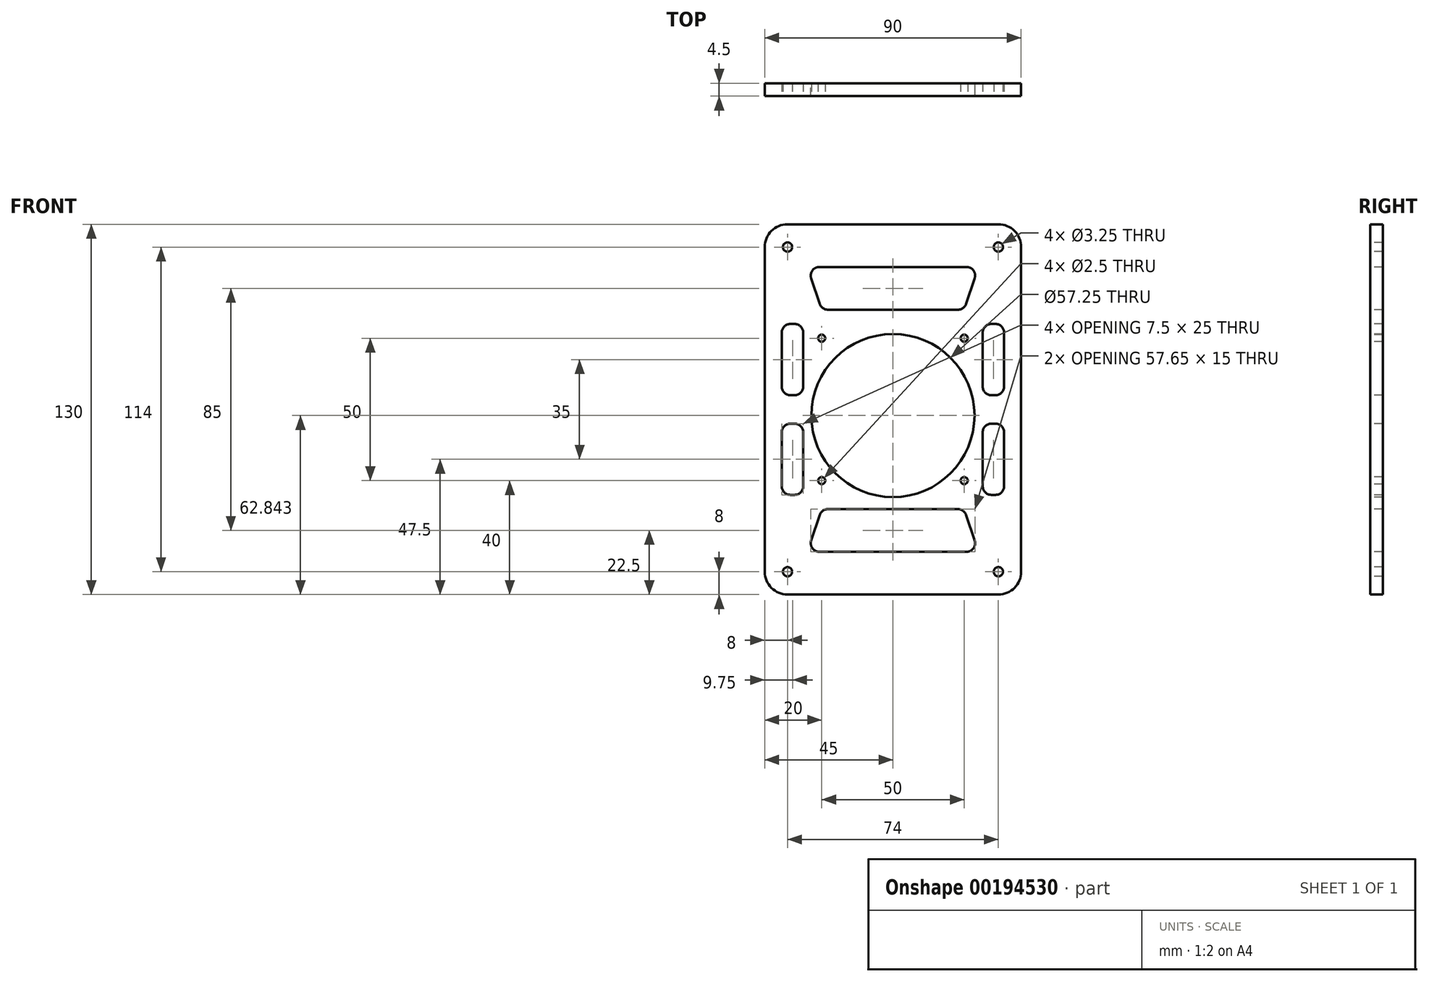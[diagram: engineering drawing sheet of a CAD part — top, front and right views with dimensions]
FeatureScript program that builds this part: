
annotation { "Feature Type Name" : "Feature", "Feature Type Description" : "" }
export const myFeature = defineFeature(function(context is Context, id is Id, definition is map)
    precondition{}
    {
        {
            var Q0;
            Q0=qCreatedBy(makeId("Front.planeOp"),FACE);
            var sketch = newSketch(context, id + "F0", { "sketchPlane" : qUnion([Q0])});
            skLineSegment(sketch, "E0.bottom", {"start": v(45, 65) * mm, "end": v(-45, 65) * mm});
            skLineSegment(sketch, "E0.top", {"start": v(45, -65) * mm, "end": v(-45, -65) * mm});
            skLineSegment(sketch, "E0.left", {"start": v(45, 65) * mm, "end": v(45, -65) * mm});
            skLineSegment(sketch, "E0.right", {"start": v(-45, 65) * mm, "end": v(-45, -65) * mm});
            skPoint(sketch, "E0.middle", {"position": v(0, 0) * mm});
            skSolve(sketch);
        }
        {
            var Q0;
            Q0 = qSketchRegion(id + "F0", true);
            extrude(context, id + "F1", {"entities" : qUnion([Q0]), "oppositeDirection" : true, "depth" : 4.5 * mm});
        }
        {
            var Q0;
            Q0=makeQuery(id+"F1.opExtrude","SWEPT_EDGE",EDGE,{"disambiguationData":[OSD([sQuery(id+"F0.wireOp",EDGE,"E0.bottom"),sQuery(id+"F0.wireOp",EDGE,"E0.left")])]});
            var Q1;
            Q1=makeQuery(id+"F1.opExtrude","SWEPT_EDGE",EDGE,{"disambiguationData":[OSD([sQuery(id+"F0.wireOp",EDGE,"E0.top"),sQuery(id+"F0.wireOp",EDGE,"E0.left")])]});
            var Q2;
            Q2=makeQuery(id+"F1.opExtrude","SWEPT_EDGE",EDGE,{"disambiguationData":[OSD([sQuery(id+"F0.wireOp",EDGE,"E0.top"),sQuery(id+"F0.wireOp",EDGE,"E0.right")])]});
            var Q3;
            Q3=makeQuery(id+"F1.opExtrude","SWEPT_EDGE",EDGE,{"disambiguationData":[OSD([sQuery(id+"F0.wireOp",EDGE,"E0.bottom"),sQuery(id+"F0.wireOp",EDGE,"E0.right")])]});
            fillet(context, id + "F2", {"entities" : qUnion([Q0, Q1, Q2, Q3]), "radius" : 8 * mm, "tangentPropagation" : true, "allowEdgeOverflow" : false});
        }
        {
            var Q0;
            Q0=qCreatedBy(makeId("Front.planeOp"),FACE);
            var sketch = newSketch(context, id + "F3", { "sketchPlane" : qUnion([Q0])});
            skCircle(sketch, "E1", {"center": v(0, -2.16) * mm, "radius": 28.62 * mm});
            skSolve(sketch);
        }
        {
            var Q0;
            Q0 = qSketchRegion(id + "F3", true);
            extrude(context, id + "F4", {"entities" : qUnion([Q0]), "operationType" : NewBodyOperationType.REMOVE, "endBound" : BoundingType.THROUGH_ALL, "oppositeDirection" : true, "depth" : 25.4 * mm});
        }
        {
            var Q0;
            Q0=qCreatedBy(makeId("Front.planeOp"),FACE);
            var sketch = newSketch(context, id + "F5", { "sketchPlane" : qUnion([Q0])});
            skCircle(sketch, "E2", {"center": v(-37, 57) * mm, "radius": 1.63 * mm});
            skCircle(sketch, "E3", {"center": v(37, 57) * mm, "radius": 1.62 * mm});
            skCircle(sketch, "E4", {"center": v(-37, -57) * mm, "radius": 1.62 * mm});
            skCircle(sketch, "E5", {"center": v(37, -57) * mm, "radius": 1.62 * mm});
            skSolve(sketch);
        }
        {
            var Q0;
            Q0 = qSketchRegion(id + "F5", true);
            extrude(context, id + "F6", {"entities" : qUnion([Q0]), "operationType" : NewBodyOperationType.REMOVE, "endBound" : BoundingType.THROUGH_ALL, "oppositeDirection" : true, "depth" : 25.4 * mm});
        }
        {
            var Q0;
            Q0=qCreatedBy(makeId("Front.planeOp"),FACE);
            var sketch = newSketch(context, id + "F7", { "sketchPlane" : qUnion([Q0])});
            skCircle(sketch, "E6", {"center": v(-25, 25) * mm, "radius": 1.25 * mm});
            skCircle(sketch, "E7", {"center": v(25, 25) * mm, "radius": 1.25 * mm});
            skCircle(sketch, "E8", {"center": v(-25, -25) * mm, "radius": 1.25 * mm});
            skCircle(sketch, "E9", {"center": v(25, -25) * mm, "radius": 1.25 * mm});
            skSolve(sketch);
        }
        {
            var Q0;
            Q0 = qSketchRegion(id + "F7", true);
            extrude(context, id + "F8", {"entities" : qUnion([Q0]), "operationType" : NewBodyOperationType.REMOVE, "endBound" : BoundingType.THROUGH_ALL, "oppositeDirection" : true, "depth" : 25.4 * mm});
        }
        {
            var Q0;
            Q0=qCreatedBy(makeId("Front.planeOp"),FACE);
            var sketch = newSketch(context, id + "F9", { "sketchPlane" : qUnion([Q0])});
            skLineSegment(sketch, "E10", {"start": v(-30, 50) * mm, "end": v(30, 50) * mm});
            skLineSegment(sketch, "E11", {"start": v(30, 50) * mm, "end": v(25, 35) * mm});
            skLineSegment(sketch, "E12", {"start": v(25, 35) * mm, "end": v(-25, 35) * mm});
            skLineSegment(sketch, "E13", {"start": v(-25, 35) * mm, "end": v(-30, 50) * mm});
            skLineSegment(sketch, "E14.bottom", {"start": v(31.5, 30) * mm, "end": v(39, 30) * mm});
            skLineSegment(sketch, "E14.top", {"start": v(31.5, 5) * mm, "end": v(39, 5) * mm});
            skLineSegment(sketch, "E14.left", {"start": v(31.5, 30) * mm, "end": v(31.5, 5) * mm});
            skLineSegment(sketch, "E14.right", {"start": v(39, 30) * mm, "end": v(39, 5) * mm});
            skLineSegment(sketch, "E15.MirrorCS", {"start": v(-39, 30) * mm, "end": v(-39, 5) * mm});
            skLineSegment(sketch, "E16.MirrorCS", {"start": v(-31.5, 30) * mm, "end": v(-31.5, 5) * mm});
            skLineSegment(sketch, "E17.MirrorCS", {"start": v(-31.5, 5) * mm, "end": v(-39, 5) * mm});
            skLineSegment(sketch, "E18.MirrorCS", {"start": v(-31.5, 30) * mm, "end": v(-39, 30) * mm});
            skLineSegment(sketch, "E19.MirrorCS", {"start": v(31.5, -5) * mm, "end": v(39, -5) * mm});
            skLineSegment(sketch, "E20.MirrorCS", {"start": v(31.5, -30) * mm, "end": v(39, -30) * mm});
            skLineSegment(sketch, "E21.MirrorCS", {"start": v(-31.5, -5) * mm, "end": v(-39, -5) * mm});
            skLineSegment(sketch, "E22.MirrorCS", {"start": v(-31.5, -30) * mm, "end": v(-39, -30) * mm});
            skLineSegment(sketch, "E23.MirrorCS", {"start": v(25, -35) * mm, "end": v(-25, -35) * mm});
            skLineSegment(sketch, "E24.MirrorCS", {"start": v(30, -50) * mm, "end": v(25, -35) * mm});
            skLineSegment(sketch, "E25.MirrorCS", {"start": v(-30, -50) * mm, "end": v(30, -50) * mm});
            skLineSegment(sketch, "E26.MirrorCS", {"start": v(-39, -30) * mm, "end": v(-39, -5) * mm});
            skLineSegment(sketch, "E27.MirrorCS", {"start": v(39, -30) * mm, "end": v(39, -5) * mm});
            skLineSegment(sketch, "E28.MirrorCS", {"start": v(31.5, -30) * mm, "end": v(31.5, -5) * mm});
            skLineSegment(sketch, "E29.MirrorCS", {"start": v(-31.5, -30) * mm, "end": v(-31.5, -5) * mm});
            skLineSegment(sketch, "E30.MirrorCS", {"start": v(-25, -35) * mm, "end": v(-30, -50) * mm});
            skSolve(sketch);
        }
        {
            var Q0;
            Q0=makeQuery(id+"F9.imprint","IMPRINT",FACE,{"disambiguationData":[TD([[makeQuery(id+"F9.imprint","IMPRINT",EDGE,{"derivedFrom":sQuery(id+"F9.wireOp",EDGE,"E10")}),-1.0]])]});
            var Q1;
            Q1=makeQuery(id+"F9.imprint","IMPRINT",FACE,{"disambiguationData":[TD([[makeQuery(id+"F9.imprint","IMPRINT",EDGE,{"derivedFrom":sQuery(id+"F9.wireOp",EDGE,"E14.bottom")}),-1.0]])]});
            var Q2;
            Q2=makeQuery(id+"F9.imprint","IMPRINT",FACE,{"disambiguationData":[TD([[makeQuery(id+"F9.imprint","IMPRINT",EDGE,{"derivedFrom":sQuery(id+"F9.wireOp",EDGE,"E19.MirrorCS")}),-1.0]])]});
            var Q3;
            Q3=makeQuery(id+"F9.imprint","IMPRINT",FACE,{"disambiguationData":[TD([[makeQuery(id+"F9.imprint","IMPRINT",EDGE,{"derivedFrom":sQuery(id+"F9.wireOp",EDGE,"E23.MirrorCS")}),1.0]])]});
            var Q4;
            Q4=makeQuery(id+"F9.imprint","IMPRINT",FACE,{"disambiguationData":[TD([[makeQuery(id+"F9.imprint","IMPRINT",EDGE,{"derivedFrom":sQuery(id+"F9.wireOp",EDGE,"E21.MirrorCS")}),1.0]])]});
            var Q5;
            Q5=makeQuery(id+"F9.imprint","IMPRINT",FACE,{"disambiguationData":[TD([[makeQuery(id+"F9.imprint","IMPRINT",EDGE,{"derivedFrom":sQuery(id+"F9.wireOp",EDGE,"E15.MirrorCS")}),1.0]])]});
            extrude(context, id + "F10", {"entities" : qUnion([Q0, Q1, Q2, Q3, Q4, Q5]), "operationType" : NewBodyOperationType.REMOVE, "endBound" : BoundingType.THROUGH_ALL, "oppositeDirection" : true, "depth" : 25.4 * mm});
        }
        {
            var Q0;
            Q0=makeQuery(id+"F10.boolean.opBoolean","COPY",EDGE,{"derivedFrom":makeQuery(id+"F10.opExtrude","SWEPT_EDGE",EDGE,{"disambiguationData":[OSD([sQuery(id+"F9.wireOp",EDGE,"E15.MirrorCS"),sQuery(id+"F9.wireOp",EDGE,"E17.MirrorCS")])]})});
            var Q1;
            Q1=makeQuery(id+"F10.boolean.opBoolean","COPY",EDGE,{"derivedFrom":makeQuery(id+"F10.opExtrude","SWEPT_EDGE",EDGE,{"disambiguationData":[OSD([sQuery(id+"F9.wireOp",EDGE,"E22.MirrorCS"),sQuery(id+"F9.wireOp",EDGE,"E26.MirrorCS")])]})});
            var Q2;
            Q2=makeQuery(id+"F10.boolean.opBoolean","COPY",EDGE,{"derivedFrom":makeQuery(id+"F10.opExtrude","SWEPT_EDGE",EDGE,{"disambiguationData":[OSD([sQuery(id+"F9.wireOp",EDGE,"E25.MirrorCS"),sQuery(id+"F9.wireOp",EDGE,"E30.MirrorCS")])]})});
            var Q3;
            Q3=makeQuery(id+"F10.boolean.opBoolean","COPY",EDGE,{"derivedFrom":makeQuery(id+"F10.opExtrude","SWEPT_EDGE",EDGE,{"disambiguationData":[OSD([sQuery(id+"F9.wireOp",EDGE,"E12"),sQuery(id+"F9.wireOp",EDGE,"E13")])]})});
            var Q4;
            Q4=makeQuery(id+"F10.boolean.opBoolean","COPY",EDGE,{"derivedFrom":makeQuery(id+"F10.opExtrude","SWEPT_EDGE",EDGE,{"disambiguationData":[OSD([sQuery(id+"F9.wireOp",EDGE,"E14.top"),sQuery(id+"F9.wireOp",EDGE,"E14.left")])]})});
            var Q5;
            Q5=makeQuery(id+"F10.boolean.opBoolean","COPY",EDGE,{"derivedFrom":makeQuery(id+"F10.opExtrude","SWEPT_EDGE",EDGE,{"disambiguationData":[OSD([sQuery(id+"F9.wireOp",EDGE,"E20.MirrorCS"),sQuery(id+"F9.wireOp",EDGE,"E28.MirrorCS")])]})});
            var Q6;
            Q6=makeQuery(id+"F10.boolean.opBoolean","COPY",EDGE,{"derivedFrom":makeQuery(id+"F10.opExtrude","SWEPT_EDGE",EDGE,{"disambiguationData":[OSD([sQuery(id+"F9.wireOp",EDGE,"E20.MirrorCS"),sQuery(id+"F9.wireOp",EDGE,"E27.MirrorCS")])]})});
            var Q7;
            Q7=makeQuery(id+"F10.boolean.opBoolean","COPY",EDGE,{"derivedFrom":makeQuery(id+"F10.opExtrude","SWEPT_EDGE",EDGE,{"disambiguationData":[OSD([sQuery(id+"F9.wireOp",EDGE,"E14.top"),sQuery(id+"F9.wireOp",EDGE,"E14.right")])]})});
            var Q8;
            Q8=makeQuery(id+"F10.boolean.opBoolean","COPY",EDGE,{"derivedFrom":makeQuery(id+"F10.opExtrude","SWEPT_EDGE",EDGE,{"disambiguationData":[OSD([sQuery(id+"F9.wireOp",EDGE,"E11"),sQuery(id+"F9.wireOp",EDGE,"E12")])]})});
            var Q9;
            Q9=makeQuery(id+"F10.boolean.opBoolean","COPY",EDGE,{"derivedFrom":makeQuery(id+"F10.opExtrude","SWEPT_EDGE",EDGE,{"disambiguationData":[OSD([sQuery(id+"F9.wireOp",EDGE,"E24.MirrorCS"),sQuery(id+"F9.wireOp",EDGE,"E25.MirrorCS")])]})});
            var Q10;
            Q10=makeQuery(id+"F10.boolean.opBoolean","COPY",EDGE,{"derivedFrom":makeQuery(id+"F10.opExtrude","SWEPT_EDGE",EDGE,{"disambiguationData":[OSD([sQuery(id+"F9.wireOp",EDGE,"E14.bottom"),sQuery(id+"F9.wireOp",EDGE,"E14.right")])]})});
            var Q11;
            Q11=makeQuery(id+"F10.boolean.opBoolean","COPY",EDGE,{"derivedFrom":makeQuery(id+"F10.opExtrude","SWEPT_EDGE",EDGE,{"disambiguationData":[OSD([sQuery(id+"F9.wireOp",EDGE,"E19.MirrorCS"),sQuery(id+"F9.wireOp",EDGE,"E27.MirrorCS")])]})});
            var Q12;
            Q12=makeQuery(id+"F10.boolean.opBoolean","COPY",EDGE,{"derivedFrom":makeQuery(id+"F10.opExtrude","SWEPT_EDGE",EDGE,{"disambiguationData":[OSD([sQuery(id+"F9.wireOp",EDGE,"E23.MirrorCS"),sQuery(id+"F9.wireOp",EDGE,"E24.MirrorCS")])]})});
            var Q13;
            Q13=makeQuery(id+"F10.boolean.opBoolean","COPY",EDGE,{"derivedFrom":makeQuery(id+"F10.opExtrude","SWEPT_EDGE",EDGE,{"disambiguationData":[OSD([sQuery(id+"F9.wireOp",EDGE,"E19.MirrorCS"),sQuery(id+"F9.wireOp",EDGE,"E28.MirrorCS")])]})});
            var Q14;
            Q14=makeQuery(id+"F10.boolean.opBoolean","COPY",EDGE,{"derivedFrom":makeQuery(id+"F10.opExtrude","SWEPT_EDGE",EDGE,{"disambiguationData":[OSD([sQuery(id+"F9.wireOp",EDGE,"E14.bottom"),sQuery(id+"F9.wireOp",EDGE,"E14.left")])]})});
            var Q15;
            Q15=makeQuery(id+"F10.boolean.opBoolean","COPY",EDGE,{"derivedFrom":makeQuery(id+"F10.opExtrude","SWEPT_EDGE",EDGE,{"disambiguationData":[OSD([sQuery(id+"F9.wireOp",EDGE,"E10"),sQuery(id+"F9.wireOp",EDGE,"E13")])]})});
            var Q16;
            Q16=makeQuery(id+"F10.boolean.opBoolean","COPY",EDGE,{"derivedFrom":makeQuery(id+"F10.opExtrude","SWEPT_EDGE",EDGE,{"disambiguationData":[OSD([sQuery(id+"F9.wireOp",EDGE,"E10"),sQuery(id+"F9.wireOp",EDGE,"E11")])]})});
            var Q17;
            Q17=makeQuery(id+"F10.boolean.opBoolean","COPY",EDGE,{"derivedFrom":makeQuery(id+"F10.opExtrude","SWEPT_EDGE",EDGE,{"disambiguationData":[OSD([sQuery(id+"F9.wireOp",EDGE,"E23.MirrorCS"),sQuery(id+"F9.wireOp",EDGE,"E30.MirrorCS")])]})});
            var Q18;
            Q18=makeQuery(id+"F10.boolean.opBoolean","COPY",EDGE,{"derivedFrom":makeQuery(id+"F10.opExtrude","SWEPT_EDGE",EDGE,{"disambiguationData":[OSD([sQuery(id+"F9.wireOp",EDGE,"E21.MirrorCS"),sQuery(id+"F9.wireOp",EDGE,"E26.MirrorCS")])]})});
            var Q19;
            Q19=makeQuery(id+"F10.boolean.opBoolean","COPY",EDGE,{"derivedFrom":makeQuery(id+"F10.opExtrude","SWEPT_EDGE",EDGE,{"disambiguationData":[OSD([sQuery(id+"F9.wireOp",EDGE,"E15.MirrorCS"),sQuery(id+"F9.wireOp",EDGE,"E18.MirrorCS")])]})});
            var Q20;
            Q20=makeQuery(id+"F10.boolean.opBoolean","COPY",EDGE,{"derivedFrom":makeQuery(id+"F10.opExtrude","SWEPT_EDGE",EDGE,{"disambiguationData":[OSD([sQuery(id+"F9.wireOp",EDGE,"E16.MirrorCS"),sQuery(id+"F9.wireOp",EDGE,"E18.MirrorCS")])]})});
            var Q21;
            Q21=makeQuery(id+"F10.boolean.opBoolean","COPY",EDGE,{"derivedFrom":makeQuery(id+"F10.opExtrude","SWEPT_EDGE",EDGE,{"disambiguationData":[OSD([sQuery(id+"F9.wireOp",EDGE,"E21.MirrorCS"),sQuery(id+"F9.wireOp",EDGE,"E29.MirrorCS")])]})});
            var Q22;
            Q22=makeQuery(id+"F10.boolean.opBoolean","COPY",EDGE,{"derivedFrom":makeQuery(id+"F10.opExtrude","SWEPT_EDGE",EDGE,{"disambiguationData":[OSD([sQuery(id+"F9.wireOp",EDGE,"E22.MirrorCS"),sQuery(id+"F9.wireOp",EDGE,"E29.MirrorCS")])]})});
            var Q23;
            Q23=makeQuery(id+"F10.boolean.opBoolean","COPY",EDGE,{"derivedFrom":makeQuery(id+"F10.opExtrude","SWEPT_EDGE",EDGE,{"disambiguationData":[OSD([sQuery(id+"F9.wireOp",EDGE,"E16.MirrorCS"),sQuery(id+"F9.wireOp",EDGE,"E17.MirrorCS")])]})});
            fillet(context, id + "F11", {"entities" : qUnion([Q0, Q1, Q2, Q3, Q4, Q5, Q6, Q7, Q8, Q9, Q10, Q11, Q12, Q13, Q14, Q15, Q16, Q17, Q18, Q19, Q20, Q21, Q22, Q23]), "radius" : 3 * mm, "tangentPropagation" : true, "allowEdgeOverflow" : false});
        }
    });
